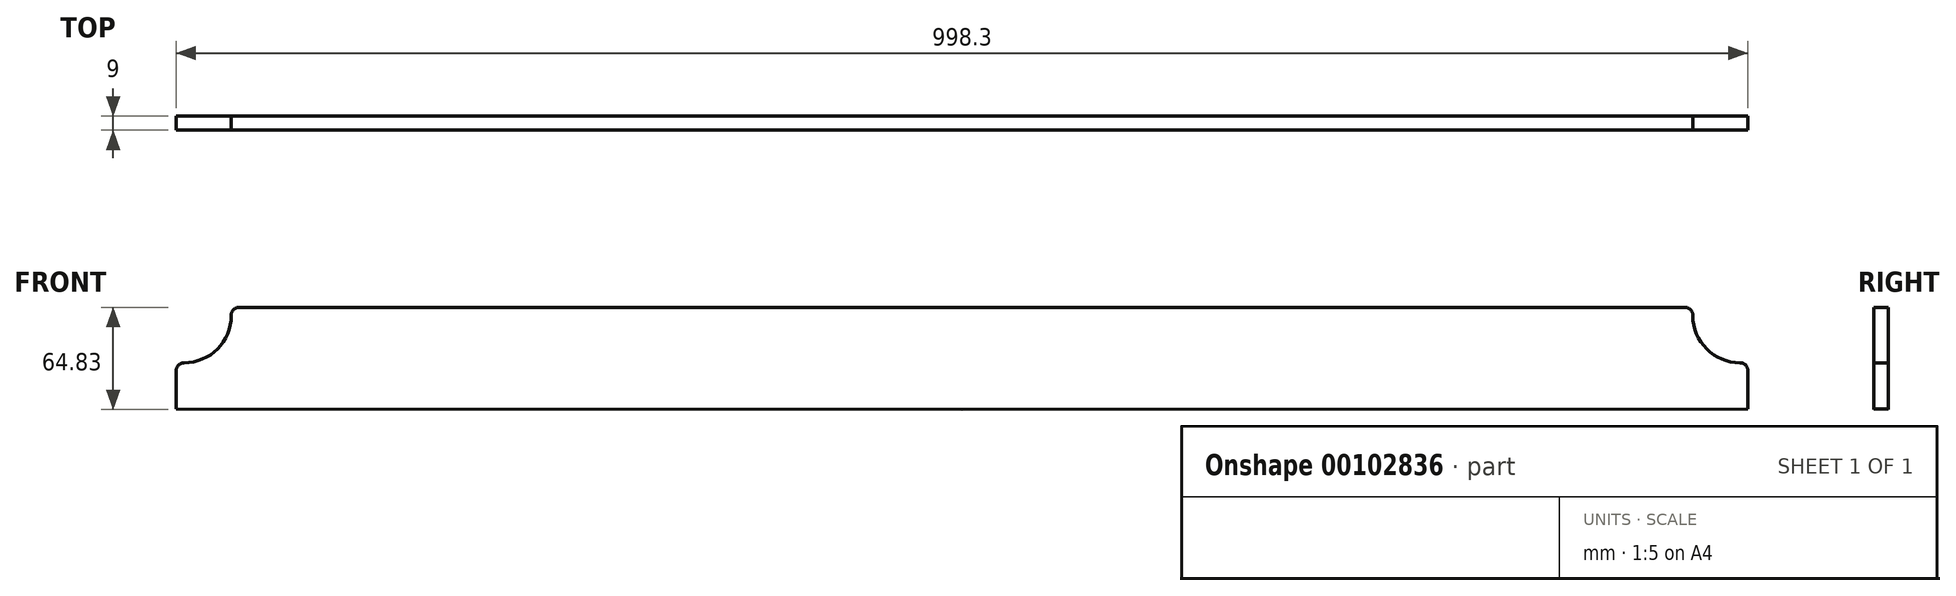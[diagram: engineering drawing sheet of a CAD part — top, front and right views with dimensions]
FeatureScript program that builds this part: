
annotation { "Feature Type Name" : "Feature", "Feature Type Description" : "" }
export const myFeature = defineFeature(function(context is Context, id is Id, definition is map)
    precondition{}
    {
        {
            var Q0;
            Q0=qCreatedBy(makeId("Front.planeOp"),FACE);
            var sketch = newSketch(context, id + "F0", { "sketchPlane" : qUnion([Q0])});
            skLineSegment(sketch, "E0.bottom", {"start": v(-500, 500) * mm, "end": v(500, 500) * mm});
            skLineSegment(sketch, "E0.top", {"start": v(-500, -500) * mm, "end": v(500, -500) * mm});
            skLineSegment(sketch, "E0.left", {"start": v(-500, 500) * mm, "end": v(-500, -500) * mm});
            skLineSegment(sketch, "E0.right", {"start": v(500, 500) * mm, "end": v(500, -500) * mm});
            skPoint(sketch, "E0.middle", {"position": v(0, 0) * mm});
            skPoint(sketch, "E1.endSnap0", {"position": v(0, -500) * mm});
            skLineSegment(sketch, "E2", {"start": v(500, -283.32) * mm, "end": v(500, -500) * mm});
            skSolve(sketch);
        }
        {
            var Q0;
            Q0=qCreatedBy(makeId("Right.planeOp"),FACE);
            var sketch = newSketch(context, id + "F1", { "sketchPlane" : qUnion([Q0])});
            skLineSegment(sketch, "E3.bottom", {"start": v(-500, -500) * mm, "end": v(500, -500) * mm});
            skLineSegment(sketch, "E3.top", {"start": v(-500, 500) * mm, "end": v(500, 500) * mm});
            skLineSegment(sketch, "E3.left", {"start": v(-500, -500) * mm, "end": v(-500, 500) * mm});
            skLineSegment(sketch, "E3.right", {"start": v(500, -500) * mm, "end": v(500, 500) * mm});
            skPoint(sketch, "E3.middle", {"position": v(0, 0) * mm});
            skSolve(sketch);
        }
        {
            var Q0;
            Q0=makeQuery(id+"F0.imprint","IMPRINT",FACE,{"disambiguationData":[TD([[makeQuery(id+"F0.imprint","IMPRINT",EDGE,{"derivedFrom":sQuery(id+"F0.wireOp",EDGE,"E0.bottom")}),-1.0]])]});
            var sketch = newSketch(context, id + "F2", { "sketchPlane" : qUnion([Q0])});
            skLineSegment(sketch, "E4", {"start": v(499.15, -475.4) * mm, "end": v(499.15, -499.74) * mm});
            skLineSegment(sketch, "E5", {"start": v(499.15, -499.74) * mm, "end": v(0, -500) * mm});
            skLineSegment(sketch, "E6", {"start": v(464.15, -440.17) * mm, "end": v(464.15, -440.4) * mm});
            skLineSegment(sketch, "E7", {"start": v(494.15, -470.4) * mm, "end": v(494.15, -470.4) * mm});
            skPoint(sketch, "E8.visualSharp", {"position": v(464.15, -470.4) * mm});
            skArc(sketch, "E8.filletArc", {"start": v(464.15, -440.4) * mm, "mid": v(472.94, -461.61) * mm, "end": v(494.15, -470.4) * mm});
            skPoint(sketch, "E9.visualSharp", {"position": v(464.15, -435.17) * mm});
            skArc(sketch, "E9.filletArc", {"start": v(464.15, -440.17) * mm, "mid": v(462.68, -436.63) * mm, "end": v(459.15, -435.17) * mm});
            skPoint(sketch, "E10.visualSharp", {"position": v(499.15, -470.4) * mm});
            skArc(sketch, "E10.filletArc", {"start": v(499.15, -475.4) * mm, "mid": v(497.68, -471.86) * mm, "end": v(494.15, -470.4) * mm});
            skLineSegment(sketch, "E11", {"start": v(459.15, -435.17) * mm, "end": v(0, -435.17) * mm});
            skArc(sketch, "E12.MirrorCS", {"start": v(-464.15, -440.17) * mm, "mid": v(-462.68, -436.63) * mm, "end": v(-459.15, -435.17) * mm});
            skArc(sketch, "E13.MirrorCS", {"start": v(-464.15, -440.4) * mm, "mid": v(-472.94, -461.61) * mm, "end": v(-494.15, -470.4) * mm});
            skArc(sketch, "E14.MirrorCS", {"start": v(-499.15, -475.4) * mm, "mid": v(-497.68, -471.86) * mm, "end": v(-494.15, -470.4) * mm});
            skLineSegment(sketch, "E15.MirrorCS", {"start": v(-499.15, -475.4) * mm, "end": v(-499.15, -499.74) * mm});
            skLineSegment(sketch, "E16.MirrorCS", {"start": v(-464.15, -440.17) * mm, "end": v(-464.15, -440.4) * mm});
            skLineSegment(sketch, "E17.MirrorCS", {"start": v(-459.15, -435.17) * mm, "end": v(0, -435.17) * mm});
            skLineSegment(sketch, "E18", {"start": v(-499.15, -499.74) * mm, "end": v(0, -500) * mm});
            skSolve(sketch);
        }
        {
            var Q0;
            Q0=makeQuery(id+"F2.imprint","IMPRINT",FACE,{"disambiguationData":[TD([[makeQuery(id+"F2.imprint","IMPRINT",EDGE,{"derivedFrom":sQuery(id+"F2.wireOp",EDGE,"E4")}),-1.0]])]});
            extrude(context, id + "F3", {"entities" : qUnion([Q0]), "depth" : 9 * mm});
        }
    });
